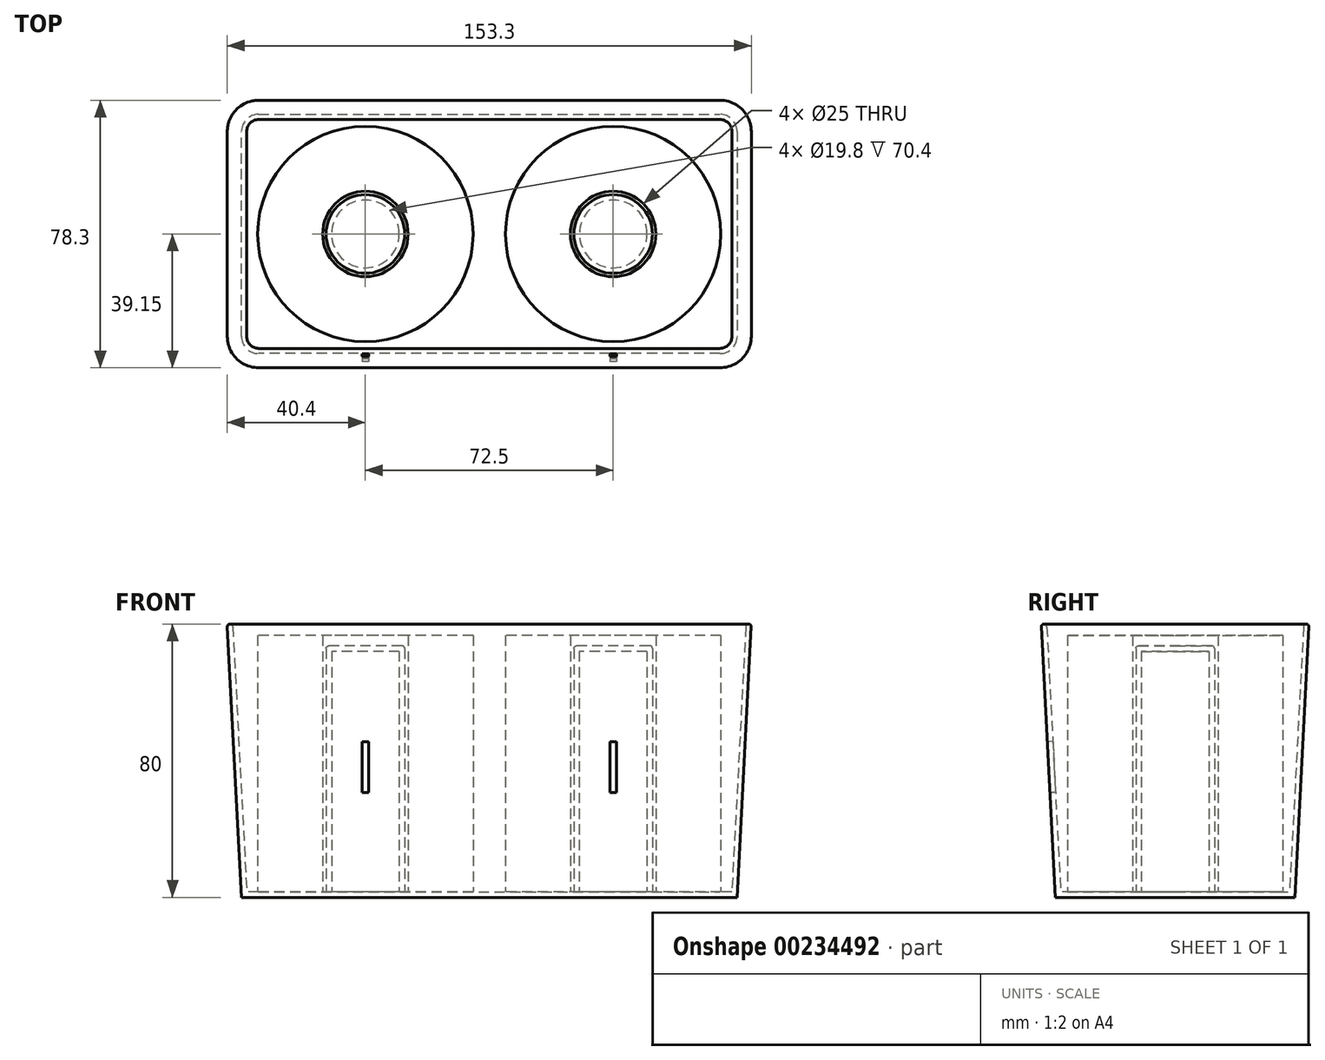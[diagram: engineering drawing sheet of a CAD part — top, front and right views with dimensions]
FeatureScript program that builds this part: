
annotation { "Feature Type Name" : "Feature", "Feature Type Description" : "" }
export const myFeature = defineFeature(function(context is Context, id is Id, definition is map)
    precondition{}
    {
        {
            assignVariable(context, id + "F0", {"name" : "Hoehe", "anyValue" : 80});
        }
        {
            assignVariable(context, id + "F1", {"name" : "Schraege", "anyValue" : 3});
        }
        {
            assignVariable(context, id + "F2", {"name" : "Wanddicke", "anyValue" : 1.6});
        }
        {
            var Q0;
            Q0=qCreatedBy(makeId("Top.planeOp"),FACE);
            var sketch = newSketch(context, id + "F3", { "sketchPlane" : qUnion([Q0])});
            skLineSegment(sketch, "E0.bottom", {"start": v(67.5, -35) * mm, "end": v(-67.5, -35) * mm});
            skLineSegment(sketch, "E0.top", {"start": v(67.5, 35) * mm, "end": v(-67.5, 35) * mm});
            skLineSegment(sketch, "E0.left", {"start": v(72.5, -30) * mm, "end": v(72.5, 30) * mm});
            skLineSegment(sketch, "E0.right", {"start": v(-72.5, -30) * mm, "end": v(-72.5, 30) * mm});
            skPoint(sketch, "E0.middle", {"position": v(0, 0) * mm});
            skPoint(sketch, "E1.visualSharp", {"position": v(-72.5, 35) * mm});
            skArc(sketch, "E1.filletArc", {"start": v(-67.5, 35) * mm, "mid": v(-71.04, 33.54) * mm, "end": v(-72.5, 30) * mm});
            skPoint(sketch, "E2.visualSharp", {"position": v(72.5, 35) * mm});
            skArc(sketch, "E2.filletArc", {"start": v(72.5, 30) * mm, "mid": v(71.04, 33.54) * mm, "end": v(67.5, 35) * mm});
            skPoint(sketch, "E3.visualSharp", {"position": v(72.5, -35) * mm});
            skArc(sketch, "E3.filletArc", {"start": v(67.5, -35) * mm, "mid": v(71.04, -33.54) * mm, "end": v(72.5, -30) * mm});
            skPoint(sketch, "E4.visualSharp", {"position": v(-72.5, -35) * mm});
            skArc(sketch, "E4.filletArc", {"start": v(-72.5, -30) * mm, "mid": v(-71.04, -33.54) * mm, "end": v(-67.5, -35) * mm});
            skSolve(sketch);
        }
        {
            var Q0;
            Q0 = qSketchRegion(id + "F3", true);
            extrude(context, id + "F4", {"entities" : qUnion([Q0]), "depth" : (getVariable(context, 'Hoehe')) * mm, "hasDraft" : true, "draftAngle" : (getVariable(context, 'Schraege')) * degree});
        }
        {
            var Q0;
            Q0=makeQuery(id+"F4.opExtrude","CAP_FACE",FACE,{"disambiguationData":[OSD([sQuery(id+"F3.wireOp",EDGE,"E0.bottom"),sQuery(id+"F3.wireOp",EDGE,"E0.top"),sQuery(id+"F3.wireOp",EDGE,"E0.left"),sQuery(id+"F3.wireOp",EDGE,"E0.right"),sQuery(id+"F3.wireOp",EDGE,"E1.filletArc"),sQuery(id+"F3.wireOp",EDGE,"E2.filletArc"),sQuery(id+"F3.wireOp",EDGE,"E3.filletArc"),sQuery(id+"F3.wireOp",EDGE,"E4.filletArc")])],"isStart":false});
            shell(context, id + "F5", {"entities" : qUnion([Q0]), "thickness" : (getVariable(context, 'Wanddicke')) * mm});
        }
        {
            var Q0;
            Q0=makeQuery(id+"F5.opShell","OFFSET_FACE",FACE,{"disambiguationData":[OSD([sQuery(id+"F3.wireOp",EDGE,"E0.bottom"),sQuery(id+"F3.wireOp",EDGE,"E0.top"),sQuery(id+"F3.wireOp",EDGE,"E0.left"),sQuery(id+"F3.wireOp",EDGE,"E0.right"),sQuery(id+"F3.wireOp",EDGE,"E1.filletArc"),sQuery(id+"F3.wireOp",EDGE,"E2.filletArc"),sQuery(id+"F3.wireOp",EDGE,"E3.filletArc"),sQuery(id+"F3.wireOp",EDGE,"E4.filletArc")])]});
            var sketch = newSketch(context, id + "F6", { "sketchPlane" : qUnion([Q0])});
            skCircle(sketch, "E5", {"center": v(-36.25, 0) * mm, "radius": 11.5 * mm});
            skCircle(sketch, "E6", {"center": v(36.25, 0) * mm, "radius": 11.5 * mm});
            skSolve(sketch);
        }
        {
            var Q0;
            Q0 = qSketchRegion(id + "F6", true);
            extrude(context, id + "F7", {"entities" : qUnion([Q0]), "depth" : (getVariable(context, 'Hoehe') * 0.9) * mm});
        }
        {
            var Q0;
            Q0=makeQuery(id+"F7.opExtrude","CAP_FACE",FACE,{"disambiguationData":[OSD([sQuery(id+"F6.wireOp",EDGE,"E5")])],"isStart":true});
            var Q1;
            Q1=makeQuery(id+"F7.opExtrude","CAP_FACE",FACE,{"disambiguationData":[OSD([sQuery(id+"F6.wireOp",EDGE,"E6")])],"isStart":true});
            shell(context, id + "F8", {"entities" : qUnion([Q0, Q1]), "thickness" : (getVariable(context, 'Wanddicke')) * mm});
        }
        {
            var Q0;
            Q0=makeQuery(id+"F4.opExtrude","CAP_FACE",FACE,{"disambiguationData":[OSD([sQuery(id+"F3.wireOp",EDGE,"E0.bottom"),sQuery(id+"F3.wireOp",EDGE,"E0.top"),sQuery(id+"F3.wireOp",EDGE,"E0.left"),sQuery(id+"F3.wireOp",EDGE,"E0.right"),sQuery(id+"F3.wireOp",EDGE,"E1.filletArc"),sQuery(id+"F3.wireOp",EDGE,"E2.filletArc"),sQuery(id+"F3.wireOp",EDGE,"E3.filletArc"),sQuery(id+"F3.wireOp",EDGE,"E4.filletArc")])],"isStart":false});
            var Q1;
            Q1=makeQuery(id+"F7.opExtrude","CAP_EDGE",EDGE,{"disambiguationData":[OSD([sQuery(id+"F6.wireOp",EDGE,"E5")])],"isStart":false});
            var Q2;
            Q2=makeQuery(id+"F7.opExtrude","CAP_EDGE",EDGE,{"disambiguationData":[OSD([sQuery(id+"F6.wireOp",EDGE,"E6")])],"isStart":false});
            fillet(context, id + "F9", {"entities" : qUnion([Q0, Q1, Q2]), "radius" : (getVariable(context, 'Wanddicke') / 2) * mm, "tangentPropagation" : true, "allowEdgeOverflow" : false});
        }
        {
            var Q0;
            Q0=makeQuery(id+"F4.opExtrude","SWEPT_BODY",BODY,{"disambiguationData":[OSD([sQuery(id+"F3.wireOp",EDGE,"E0.bottom"),sQuery(id+"F3.wireOp",EDGE,"E0.top"),sQuery(id+"F3.wireOp",EDGE,"E0.left"),sQuery(id+"F3.wireOp",EDGE,"E0.right"),sQuery(id+"F3.wireOp",EDGE,"E1.filletArc"),sQuery(id+"F3.wireOp",EDGE,"E2.filletArc"),sQuery(id+"F3.wireOp",EDGE,"E3.filletArc"),sQuery(id+"F3.wireOp",EDGE,"E4.filletArc")])]});
            var Q1;
            Q1=makeQuery(id+"F7.opExtrude","SWEPT_BODY",BODY,{"disambiguationData":[OSD([sQuery(id+"F6.wireOp",EDGE,"E5")])]});
            var Q2;
            Q2=makeQuery(id+"F7.opExtrude","SWEPT_BODY",BODY,{"disambiguationData":[OSD([sQuery(id+"F6.wireOp",EDGE,"E6")])]});
            booleanBodies(context, id + "F10", {"operationType" : BooleanOperationType.UNION, "tools" : qUnion([Q0, Q1, Q2])});
        }
        {
            var Q0;
            {var subQ0=sQuery(id+"F3.wireOp",EDGE,"E0.right");var subQ1=sQuery(id+"F3.wireOp",EDGE,"E0.left");var subQ2=sQuery(id+"F3.wireOp",EDGE,"E0.top");var subQ3=sQuery(id+"F3.wireOp",EDGE,"E0.bottom");var subQ4=sQuery(id+"F3.wireOp",EDGE,"E1.filletArc");var subQ5=sQuery(id+"F3.wireOp",EDGE,"E2.filletArc");var subQ6=sQuery(id+"F3.wireOp",EDGE,"E3.filletArc");var subQ7=sQuery(id+"F3.wireOp",EDGE,"E4.filletArc");Q0=makeQuery(id+"F10.opBoolean","SPLIT",FACE,{"disambiguationData":[TD([makeQuery(id+"F5.opShell","OFFSET_FACE",FACE,{"disambiguationData":[OSD([subQ3])]})])],"derivedFrom":makeQuery(id+"F5.opShell","OFFSET_FACE",FACE,{"disambiguationData":[OSD([subQ3,subQ2,subQ1,subQ0,subQ4,subQ5,subQ6,subQ7])]})});}
            var sketch = newSketch(context, id + "F11", { "sketchPlane" : qUnion([Q0])});
            skCircle(sketch, "E7.0.0", {"center": v(-36.25, 0) * mm, "radius": 10.7 * mm});
            skCircle(sketch, "E8", {"center": v(-36.25, 0) * mm, "radius": 31.5 * mm});
            skCircle(sketch, "E9", {"center": v(-36.25, 0) * mm, "radius": 12.5 * mm});
            skLineSegment(sketch, "E10", {"start": v(0, 13.9) * mm, "end": v(0, -16.18) * mm});
            skCircle(sketch, "E11.MirrorC", {"center": v(36.25, 0) * mm, "radius": 12.5 * mm});
            skCircle(sketch, "E12.MirrorC", {"center": v(36.25, 0) * mm, "radius": 31.5 * mm});
            skSolve(sketch);
        }
        {
            var Q0;
            Q0 = qSketchRegion(id + "F11", true);
            extrude(context, id + "F12", {"entities" : qUnion([Q0]), "depth" : 75 * mm});
        }
        {
            var Q0;
            Q0=makeQuery(id+"F4.opExtrude","SWEPT_FACE",FACE,{"disambiguationData":[OSD([sQuery(id+"F3.wireOp",EDGE,"E0.bottom")])]});
            var sketch = newSketch(context, id + "F13", { "sketchPlane" : qUnion([Q0])});
            skLineSegment(sketch, "E13.bottom", {"start": v(-35.25, 32.5) * mm, "end": v(-37.25, 32.5) * mm});
            skLineSegment(sketch, "E13.top", {"start": v(-35.25, 47.5) * mm, "end": v(-37.25, 47.5) * mm});
            skLineSegment(sketch, "E13.left", {"start": v(-35.25, 32.5) * mm, "end": v(-35.25, 47.5) * mm});
            skLineSegment(sketch, "E13.right", {"start": v(-37.25, 32.5) * mm, "end": v(-37.25, 47.5) * mm});
            skPoint(sketch, "E13.middle", {"position": v(-36.25, 40) * mm});
            skLineSegment(sketch, "E14.bottom", {"start": v(37.25, 32.5) * mm, "end": v(35.25, 32.5) * mm});
            skLineSegment(sketch, "E14.top", {"start": v(37.25, 47.5) * mm, "end": v(35.25, 47.5) * mm});
            skLineSegment(sketch, "E14.left", {"start": v(37.25, 32.5) * mm, "end": v(37.25, 47.5) * mm});
            skLineSegment(sketch, "E14.right", {"start": v(35.25, 32.5) * mm, "end": v(35.25, 47.5) * mm});
            skPoint(sketch, "E14.middle", {"position": v(36.25, 40) * mm});
            skLineSegment(sketch, "E15", {"start": v(0, 0) * mm, "end": v(0, 53.19) * mm, "construction": true});
            skPoint(sketch, "E15.endSnap0", {"position": v(0, 1.83) * mm});
            skSolve(sketch);
        }
        {
            var Q0;
            Q0 = qSketchRegion(id + "F13", true);
            extrude(context, id + "F14", {"entities" : qUnion([Q0]), "operationType" : NewBodyOperationType.REMOVE, "endBound" : BoundingType.UP_TO_NEXT, "oppositeDirection" : true, "depth" : 25 * mm});
        }
    });
